# Revit family: NW
name_source: partatom
category: Lighting Fixtures
revit_build: Autodesk Revit 2014 (Build: 20130308_1515(x64)
units: mm (PartAtom-declared; Revit-internal decimal feet)

## types (2) — shared parameters
Apparent Load = 2 VA
Body = Paint - Hubbell - Black Matte Textured
Certification = UL924 Damp Listed, NFPA 101 and NFPA 70
Color Filter = 16777215
Default Elevation = 48 "
Description = The NiteWay™ patient room night light is the ideal choice for the demands ofhealthcare environments. It combines an aesthetically pleasing form with lowglare performance, rugged durability and water-tight construction. NiteWay is alsosuitable for commercial, hospitality and residential applications.
Dimming Lamp Color Temperature Shift = <None>
Features = Simple, low-profile form is architecturally-pleasing and can easily be cleaned.
Available in either a vertical or horizontal orientation and with either white or amber LEDs.
No visibly exposed fasteners.
Rated for wet location environments.
Standard antimicrobial finish available in three standard colors.
Available with optional photocell control.
Glass = Glass - Hubbell - White
Lamp = LED
Manufacturer = Healthcare Solutions A unit of Hubbell Lighting
Model = Niteway
Photometric Web File = generic
Product Doucumentation Link = https://hubbellcdn.com
Product Page URL = https://www.hubbell.com
Radius = 3.35 "
Steel = Metal-Hubbell-Galvanized_Steel
Tilt Angle = 60.00°
Type Comments = Light Fixture
URL = https://www.hubbell.com
Warranty = • 5 year warranty. Please consult
factory for details
Warranty Notes = https://hubbellcdn.com
Wattage Comments = 2W

## per-type parameters (varying)
| type | Inner Length | Inner Width | Length | Width |
| NW-H | 2.8 " | 1.8 " | 5.39 " | 3.39 " |
| NW-V | 1.8 " | 2.8 " | 3.39 " | 5.39 " |

## geometry (parser evidence)
native form markers: Sweep x1
no freeform markers — native parametric forms only
